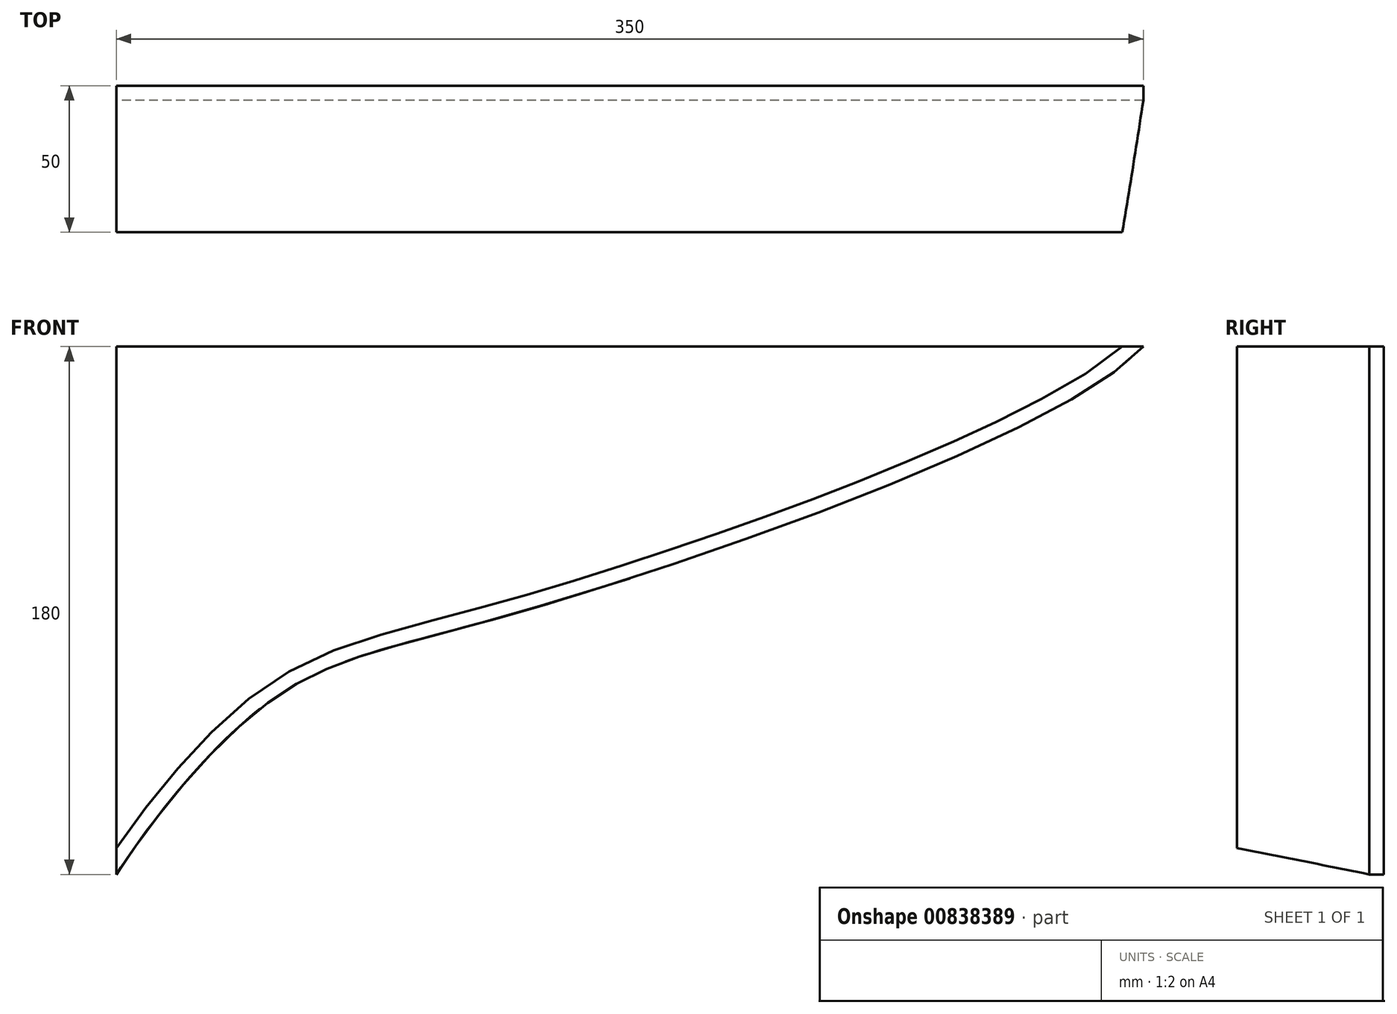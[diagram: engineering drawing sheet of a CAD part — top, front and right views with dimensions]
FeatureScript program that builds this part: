
annotation { "Feature Type Name" : "Feature", "Feature Type Description" : "" }
export const myFeature = defineFeature(function(context is Context, id is Id, definition is map)
    precondition{}
    {
        {
            var Q0;
            Q0=qCreatedBy(makeId("Front.planeOp"),FACE);
            var sketch = newSketch(context, id + "F0", { "sketchPlane" : qUnion([Q0])});
            skLineSegment(sketch, "E0", {"start": v(0, 0) * mm, "end": v(0, 180) * mm});
            skLineSegment(sketch, "E1", {"start": v(0, 180) * mm, "end": v(350, 180) * mm});
            skFitSpline(sketch, "E2", {"points": [v(0, 0) * mm, v(52.6, 59.24) * mm, v(135.5, 88.93) * mm, v(350, 180) * mm], "startDerivative": vector(138.24, 213.16) * mm, "endDerivative": vector(173.58, 192.13) * mm});
            skSolve(sketch);
        }
        {
            var Q0;
            Q0 = qSketchRegion(id + "F0", true);
            extrude(context, id + "F1", {"entities" : qUnion([Q0]), "depth" : 50 * mm, "offsetDistance" : 25 * mm});
        }
        {
            var Q0;
            Q0=makeQuery(id+"F1.opExtrude","CAP_EDGE",EDGE,{"disambiguationData":[OSD([sQuery(id+"F0.wireOp",EDGE,"E2")])],"isStart":false});
            chamfer(context, id + "F2", {"entities" : qUnion([Q0]), "chamferType" : ChamferType.TWO_OFFSETS, "width1" : 5 * mm, "oppositeDirection" : false, "width2" : 45 * mm, "tangentPropagation" : true});
        }
    });
